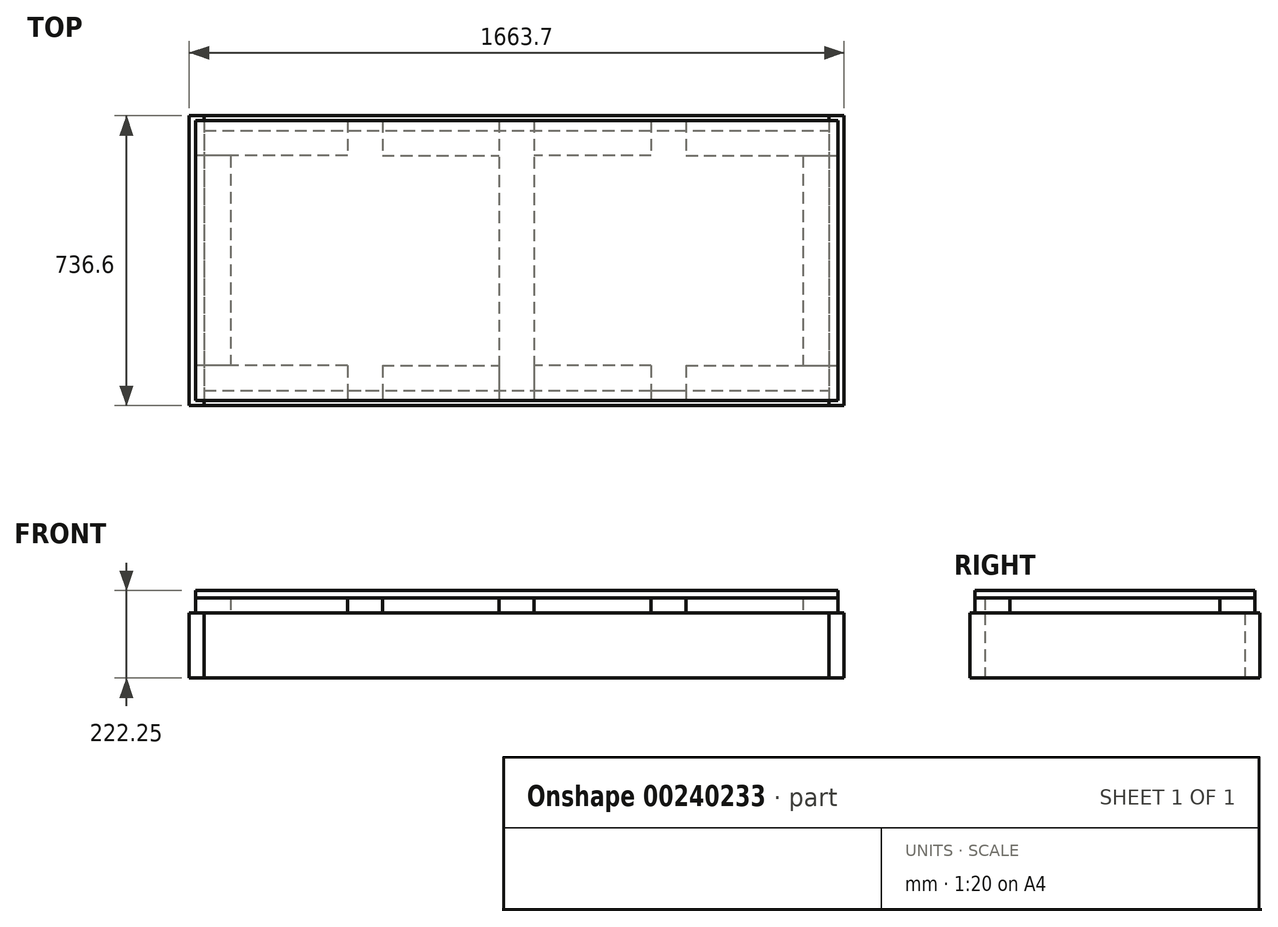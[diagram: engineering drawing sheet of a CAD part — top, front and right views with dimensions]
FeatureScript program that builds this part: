
annotation { "Feature Type Name" : "Feature", "Feature Type Description" : "" }
export const myFeature = defineFeature(function(context is Context, id is Id, definition is map)
    precondition{}
    {
        {
            var Q0;
            Q0=qCreatedBy(makeId("Top.planeOp"),FACE);
            var sketch = newSketch(context, id + "F0", { "sketchPlane" : qUnion([Q0])});
            skLineSegment(sketch, "E0.bottom", {"start": v(0, 0) * mm, "end": v(1587.5, 0) * mm});
            skLineSegment(sketch, "E0.top", {"start": v(0, -38.1) * mm, "end": v(1587.5, -38.1) * mm});
            skLineSegment(sketch, "E0.left", {"start": v(0, 0) * mm, "end": v(0, -38.1) * mm});
            skLineSegment(sketch, "E0.right", {"start": v(1587.5, 0) * mm, "end": v(1587.5, -38.1) * mm});
            skLineSegment(sketch, "E1.bottom", {"start": v(0, 698.5) * mm, "end": v(1587.5, 698.5) * mm});
            skLineSegment(sketch, "E1.top", {"start": v(0, 660.4) * mm, "end": v(1587.5, 660.4) * mm});
            skLineSegment(sketch, "E1.left", {"start": v(0, 698.5) * mm, "end": v(0, 660.4) * mm});
            skLineSegment(sketch, "E1.right", {"start": v(1587.5, 698.5) * mm, "end": v(1587.5, 660.4) * mm});
            skLineSegment(sketch, "E2.bottom", {"start": v(1587.5, 698.5) * mm, "end": v(1625.6, 698.5) * mm});
            skLineSegment(sketch, "E2.top", {"start": v(1587.5, -38.1) * mm, "end": v(1625.6, -38.1) * mm});
            skLineSegment(sketch, "E2.left", {"start": v(1587.5, 698.5) * mm, "end": v(1587.5, -38.1) * mm});
            skLineSegment(sketch, "E2.right", {"start": v(1625.6, 698.5) * mm, "end": v(1625.6, -38.1) * mm});
            skLineSegment(sketch, "E3.bottom", {"start": v(0, -38.1) * mm, "end": v(-38.1, -38.1) * mm});
            skLineSegment(sketch, "E3.top", {"start": v(0, 698.5) * mm, "end": v(-38.1, 698.5) * mm});
            skLineSegment(sketch, "E3.left", {"start": v(0, -38.1) * mm, "end": v(0, 698.5) * mm});
            skLineSegment(sketch, "E3.right", {"start": v(-38.1, -38.1) * mm, "end": v(-38.1, 698.5) * mm});
            skSolve(sketch);
        }
        {
            var Q0;
            {var subQ3=sQuery(id+"F0.wireOp",EDGE,"E3.bottom");Q0=makeQuery(id+"F0.imprint","IMPRINT",FACE,{"disambiguationData":[TD([[makeQuery(id+"F0.imprint","IMPRINT",EDGE,{"derivedFrom":subQ3}),-1.0]])]});}
            extrude(context, id + "F1", {"entities" : qUnion([Q0]), "endBound" : BoundingType.SYMMETRIC, "depth" : 165.1 * mm});
        }
        {
            var Q0;
            {var subQ0=sQuery(id+"F0.wireOp",EDGE,"E1.bottom");Q0=makeQuery(id+"F0.imprint","IMPRINT",FACE,{"disambiguationData":[TD([[makeQuery(id+"F0.imprint","IMPRINT",EDGE,{"derivedFrom":subQ0}),-1.0]])]});}
            extrude(context, id + "F2", {"entities" : qUnion([Q0]), "endBound" : BoundingType.SYMMETRIC, "depth" : 165.1 * mm});
        }
        {
            var Q0;
            {var subQ0=sQuery(id+"F0.wireOp",EDGE,"E0.bottom");Q0=makeQuery(id+"F0.imprint","IMPRINT",FACE,{"disambiguationData":[TD([[makeQuery(id+"F0.imprint","IMPRINT",EDGE,{"derivedFrom":subQ0}),-1.0]])]});}
            extrude(context, id + "F3", {"entities" : qUnion([Q0]), "endBound" : BoundingType.SYMMETRIC, "depth" : 165.1 * mm});
        }
        {
            var Q0;
            {var subQ3=sQuery(id+"F0.wireOp",EDGE,"E2.bottom");Q0=makeQuery(id+"F0.imprint","IMPRINT",FACE,{"disambiguationData":[TD([[makeQuery(id+"F0.imprint","IMPRINT",EDGE,{"derivedFrom":subQ3}),-1.0]])]});}
            extrude(context, id + "F4", {"entities" : qUnion([Q0]), "endBound" : BoundingType.SYMMETRIC, "depth" : 165.1 * mm});
        }
        {
            var Q0;
            Q0=makeQuery(id+"F3.opExtrude","CAP_FACE",FACE,{"disambiguationData":[OSD([sQuery(id+"F0.wireOp",EDGE,"E0.bottom"),sQuery(id+"F0.wireOp",EDGE,"E0.top"),sQuery(id+"F0.wireOp",EDGE,"E2.left"),sQuery(id+"F0.wireOp",EDGE,"E3.left")])],"isStart":false});
            var sketch = newSketch(context, id + "F5", { "sketchPlane" : qUnion([Q0])});
            skLineSegment(sketch, "E4.0", {"start": v(-22.23, -25.4) * mm, "end": v(-22.23, 685.8) * mm});
            skLineSegment(sketch, "E4.1", {"start": v(1609.73, -25.4) * mm, "end": v(-22.23, -25.4) * mm});
            skLineSegment(sketch, "E4.2", {"start": v(1609.73, -25.4) * mm, "end": v(1609.73, 685.8) * mm});
            skLineSegment(sketch, "E4.3", {"start": v(1609.73, 685.8) * mm, "end": v(-22.23, 685.8) * mm});
            skLineSegment(sketch, "E5", {"start": v(66.67, 596.9) * mm, "end": v(66.67, 63.5) * mm});
            skLineSegment(sketch, "E6.bottom", {"start": v(452.44, 685.8) * mm, "end": v(363.54, 685.8) * mm});
            skPoint(sketch, "E6.middle", {"position": v(793.75, 330.2) * mm});
            skLineSegment(sketch, "E7.right", {"start": v(749.3, 685.8) * mm, "end": v(749.3, -25.4) * mm});
            skLineSegment(sketch, "E8.trimOffspring", {"start": v(363.54, 63.5) * mm, "end": v(-22.23, 63.5) * mm});
            skLineSegment(sketch, "E9", {"start": v(363.54, 685.8) * mm, "end": v(363.54, -25.4) * mm});
            skLineSegment(sketch, "E10", {"start": v(452.44, 685.8) * mm, "end": v(452.44, -25.4) * mm});
            skLineSegment(sketch, "E11", {"start": v(363.54, 596.9) * mm, "end": v(-22.23, 596.9) * mm});
            skLineSegment(sketch, "E12", {"start": v(452.44, 596.9) * mm, "end": v(749.3, 596.9) * mm});
            skLineSegment(sketch, "E13", {"start": v(452.44, 63.5) * mm, "end": v(749.3, 63.5) * mm});
            skLineSegment(sketch, "E14", {"start": v(793.75, 685.8) * mm, "end": v(793.75, -25.4) * mm, "construction": true});
            skLineSegment(sketch, "E15.MirrorCS", {"start": v(1135.06, 685.8) * mm, "end": v(1223.96, 685.8) * mm});
            skLineSegment(sketch, "E16.MirrorCS", {"start": v(1135.06, 685.8) * mm, "end": v(1135.06, -25.4) * mm});
            skLineSegment(sketch, "E17.MirrorCS", {"start": v(1223.96, 685.8) * mm, "end": v(1223.96, -25.4) * mm});
            skLineSegment(sketch, "E18.MirrorCS", {"start": v(838.2, 685.8) * mm, "end": v(838.2, -25.4) * mm});
            skLineSegment(sketch, "E19.MirrorCS", {"start": v(1223.96, 63.5) * mm, "end": v(1609.73, 63.5) * mm});
            skLineSegment(sketch, "E20.MirrorCS", {"start": v(1135.06, 596.9) * mm, "end": v(838.2, 596.9) * mm});
            skLineSegment(sketch, "E21.MirrorCS", {"start": v(1135.06, 63.5) * mm, "end": v(838.2, 63.5) * mm});
            skLineSegment(sketch, "E22.MirrorCS", {"start": v(1223.96, 596.9) * mm, "end": v(1609.73, 596.9) * mm});
            skLineSegment(sketch, "E23.MirrorCS", {"start": v(1520.83, 596.9) * mm, "end": v(1520.83, 63.5) * mm});
            skLineSegment(sketch, "E24", {"start": v(-38.1, 698.5) * mm, "end": v(1625.6, -38.1) * mm, "construction": true});
            skLineSegment(sketch, "E25", {"start": v(-38.1, -38.1) * mm, "end": v(1625.6, 698.5) * mm, "construction": true});
            skLineSegment(sketch, "E26", {"start": v(1609.73, 330.2) * mm, "end": v(-22.23, 330.2) * mm, "construction": true});
            skLineSegment(sketch, "E27", {"start": v(407.99, 685.8) * mm, "end": v(407.99, -25.4) * mm, "construction": true});
            skSolve(sketch);
        }
        {
            var Q0;
            {var subQ5=sQuery(id+"F5.wireOp",EDGE,"E5");Q0=makeQuery(id+"F5.imprint","IMPRINT",FACE,{"disambiguationData":[TD([[makeQuery(id+"F5.imprint","IMPRINT",EDGE,{"derivedFrom":subQ5}),-1.0]])]});}
            extrude(context, id + "F6", {"entities" : qUnion([Q0]), "depth" : 38.1 * mm});
        }
        {
            var Q0;
            {var subQ3=sQuery(id+"F5.wireOp",EDGE,"E6.bottom");Q0=makeQuery(id+"F5.imprint","IMPRINT",FACE,{"disambiguationData":[TD([[makeQuery(id+"F5.imprint","IMPRINT",EDGE,{"derivedFrom":subQ3}),1.0]])]});}
            var Q1;
            {var subQ0=sQuery(id+"F5.wireOp",EDGE,"E9");var subQ1=sQuery(id+"F5.wireOp",EDGE,"E4.1");var subQ2=makeQuery(id+"F5.imprint","INTERSECT",VERTEX,{"derivedFrom":[subQ1,subQ0]});Q1=makeQuery(id+"F5.imprint","IMPRINT",FACE,{"disambiguationData":[TD([[makeQuery(id+"F5.imprint","IMPRINT",EDGE,{"disambiguationData":[TD([[subQ2,1.0]])],"derivedFrom":subQ1}),-1.0]])]});}
            extrude(context, id + "F7", {"entities" : qUnion([Q0, Q1]), "depth" : 38.1 * mm});
        }
        {
            var Q0;
            {var subQ0=sQuery(id+"F5.wireOp",EDGE,"E7.right");var subQ5=sQuery(id+"F5.wireOp",EDGE,"E4.3");var subQ6=makeQuery(id+"F5.imprint","INTERSECT",VERTEX,{"derivedFrom":[subQ5,subQ0]});Q0=makeQuery(id+"F5.imprint","IMPRINT",FACE,{"disambiguationData":[TD([[makeQuery(id+"F5.imprint","IMPRINT",EDGE,{"disambiguationData":[TD([[subQ6,1.0]])],"derivedFrom":subQ5}),1.0]])]});}
            var Q1;
            {var subQ0=sQuery(id+"F5.wireOp",EDGE,"E7.right");var subQ1=sQuery(id+"F5.wireOp",EDGE,"E4.1");var subQ2=makeQuery(id+"F5.imprint","INTERSECT",VERTEX,{"derivedFrom":[subQ1,subQ0]});Q1=makeQuery(id+"F5.imprint","IMPRINT",FACE,{"disambiguationData":[TD([[makeQuery(id+"F5.imprint","IMPRINT",EDGE,{"disambiguationData":[TD([[subQ2,1.0]])],"derivedFrom":subQ1}),-1.0]])]});}
            extrude(context, id + "F8", {"entities" : qUnion([Q0, Q1]), "depth" : 38.1 * mm});
        }
        {
            var Q0;
            {var subQ6=sQuery(id+"F5.wireOp",EDGE,"E15.MirrorCS");Q0=makeQuery(id+"F5.imprint","IMPRINT",FACE,{"disambiguationData":[TD([[makeQuery(id+"F5.imprint","IMPRINT",EDGE,{"derivedFrom":subQ6}),-1.0]])]});}
            var Q1;
            {var subQ0=sQuery(id+"F5.wireOp",EDGE,"E16.MirrorCS");var subQ1=sQuery(id+"F5.wireOp",EDGE,"E4.1");var subQ2=makeQuery(id+"F5.imprint","INTERSECT",VERTEX,{"derivedFrom":[subQ1,subQ0]});Q1=makeQuery(id+"F5.imprint","IMPRINT",FACE,{"disambiguationData":[TD([[makeQuery(id+"F5.imprint","IMPRINT",EDGE,{"disambiguationData":[TD([[subQ2,1.0]])],"derivedFrom":subQ1}),-1.0]])]});}
            extrude(context, id + "F9", {"entities" : qUnion([Q0, Q1]), "depth" : 38.1 * mm});
        }
        {
            var Q0;
            {var subQ5=sQuery(id+"F5.wireOp",EDGE,"E23.MirrorCS");Q0=makeQuery(id+"F5.imprint","IMPRINT",FACE,{"disambiguationData":[TD([[makeQuery(id+"F5.imprint","IMPRINT",EDGE,{"derivedFrom":subQ5}),1.0]])]});}
            extrude(context, id + "F10", {"entities" : qUnion([Q0]), "depth" : 38.1 * mm});
        }
        {
            var Q0;
            {var subQ1=sQuery(id+"F5.wireOp",EDGE,"E4.3");var subQ5=sQuery(id+"F5.wireOp",EDGE,"E4.0");var subQ6=makeQuery(id+"F5.imprint","INTERSECT",VERTEX,{"derivedFrom":[subQ5,subQ1]});Q0=makeQuery(id+"F5.imprint","IMPRINT",FACE,{"disambiguationData":[TD([[makeQuery(id+"F5.imprint","IMPRINT",EDGE,{"disambiguationData":[TD([[subQ6,1.0]])],"derivedFrom":subQ5}),-1.0]])]});}
            var Q1;
            {var subQ5=sQuery(id+"F5.wireOp",EDGE,"E12");Q1=makeQuery(id+"F5.imprint","IMPRINT",FACE,{"disambiguationData":[TD([[makeQuery(id+"F5.imprint","IMPRINT",EDGE,{"derivedFrom":subQ5}),1.0]])]});}
            var Q2;
            {var subQ5=sQuery(id+"F5.wireOp",EDGE,"E20.MirrorCS");Q2=makeQuery(id+"F5.imprint","IMPRINT",FACE,{"disambiguationData":[TD([[makeQuery(id+"F5.imprint","IMPRINT",EDGE,{"derivedFrom":subQ5}),-1.0]])]});}
            var Q3;
            {var subQ4=sQuery(id+"F5.wireOp",EDGE,"E4.3");var subQ6=sQuery(id+"F5.wireOp",EDGE,"E4.2");var subQ7=makeQuery(id+"F5.imprint","INTERSECT",VERTEX,{"derivedFrom":[subQ4,subQ6]});Q3=makeQuery(id+"F5.imprint","IMPRINT",FACE,{"disambiguationData":[TD([[makeQuery(id+"F5.imprint","IMPRINT",EDGE,{"disambiguationData":[TD([[subQ7,1.0]])],"derivedFrom":subQ6}),1.0]])]});}
            extrude(context, id + "F11", {"entities" : qUnion([Q0, Q1, Q2, Q3]), "depth" : 38.1 * mm});
        }
        {
            var Q0;
            {var subQ1=sQuery(id+"F5.wireOp",EDGE,"qj0oYwkd-f0o2-NH23-ZEer-4dDjqUlUklY0.right");Q0=makeQuery(id+"F5.imprint","IMPRINT",FACE,{"disambiguationData":[TD([[makeQuery(id+"F5.imprint","IMPRINT",EDGE,{"derivedFrom":subQ1}),-1.0]])]});}
            var Q1;
            {var subQ0=sQuery(id+"F5.wireOp",EDGE,"E9");var subQ1=sQuery(id+"F5.wireOp",EDGE,"E4.1");var subQ2=makeQuery(id+"F5.imprint","INTERSECT",VERTEX,{"derivedFrom":[subQ1,subQ0]});Q1=makeQuery(id+"F5.imprint","IMPRINT",FACE,{"disambiguationData":[TD([[makeQuery(id+"F5.imprint","IMPRINT",EDGE,{"disambiguationData":[TD([[subQ2,-1.0]])],"derivedFrom":subQ1}),-1.0]])]});}
            var Q2;
            {var subQ0=sQuery(id+"F5.wireOp",EDGE,"E13");Q2=makeQuery(id+"F5.imprint","IMPRINT",FACE,{"disambiguationData":[TD([[makeQuery(id+"F5.imprint","IMPRINT",EDGE,{"derivedFrom":subQ0}),-1.0]])]});}
            var Q3;
            {var subQ0=sQuery(id+"F5.wireOp",EDGE,"E7.right");var subQ1=sQuery(id+"F5.wireOp",EDGE,"E4.1");var subQ2=makeQuery(id+"F5.imprint","INTERSECT",VERTEX,{"derivedFrom":[subQ1,subQ0]});Q3=makeQuery(id+"F5.imprint","IMPRINT",FACE,{"disambiguationData":[TD([[makeQuery(id+"F5.imprint","IMPRINT",EDGE,{"disambiguationData":[TD([[subQ2,-1.0]])],"derivedFrom":subQ1}),-1.0]])]});}
            var Q4;
            {var subQ0=sQuery(id+"F5.wireOp",EDGE,"E21.MirrorCS");Q4=makeQuery(id+"F5.imprint","IMPRINT",FACE,{"disambiguationData":[TD([[makeQuery(id+"F5.imprint","IMPRINT",EDGE,{"derivedFrom":subQ0}),1.0]])]});}
            var Q5;
            {var subQ0=sQuery(id+"F5.wireOp",EDGE,"E16.MirrorCS");var subQ1=sQuery(id+"F5.wireOp",EDGE,"E4.1");var subQ2=makeQuery(id+"F5.imprint","INTERSECT",VERTEX,{"derivedFrom":[subQ1,subQ0]});Q5=makeQuery(id+"F5.imprint","IMPRINT",FACE,{"disambiguationData":[TD([[makeQuery(id+"F5.imprint","IMPRINT",EDGE,{"disambiguationData":[TD([[subQ2,-1.0]])],"derivedFrom":subQ1}),-1.0]])]});}
            var Q6;
            {var subQ4=sQuery(id+"F5.wireOp",EDGE,"E4.2");var subQ5=sQuery(id+"F5.wireOp",EDGE,"E4.1");var subQ6=makeQuery(id+"F5.imprint","INTERSECT",VERTEX,{"derivedFrom":[subQ5,subQ4]});Q6=makeQuery(id+"F5.imprint","IMPRINT",FACE,{"disambiguationData":[TD([[makeQuery(id+"F5.imprint","IMPRINT",EDGE,{"disambiguationData":[TD([[subQ6,-1.0]])],"derivedFrom":subQ5}),-1.0]])]});}
            var Q7;
            {var subQ0=sQuery(id+"F5.wireOp",EDGE,"E17.MirrorCS");var subQ1=sQuery(id+"F5.wireOp",EDGE,"E4.1");var subQ2=makeQuery(id+"F5.imprint","INTERSECT",VERTEX,{"derivedFrom":[subQ1,subQ0]});Q7=makeQuery(id+"F5.imprint","IMPRINT",FACE,{"disambiguationData":[TD([[makeQuery(id+"F5.imprint","IMPRINT",EDGE,{"disambiguationData":[TD([[subQ2,1.0]])],"derivedFrom":subQ1}),-1.0]])]});}
            var Q8;
            {var subQ2=sQuery(id+"F5.wireOp",EDGE,"E4.0");var subQ9=sQuery(id+"F5.wireOp",EDGE,"E4.1");var subQ11=makeQuery(id+"F5.imprint","INTERSECT",VERTEX,{"derivedFrom":[subQ2,subQ9]});Q8=makeQuery(id+"F5.imprint","IMPRINT",FACE,{"disambiguationData":[TD([[makeQuery(id+"F5.imprint","IMPRINT",EDGE,{"disambiguationData":[TD([[subQ11,-1.0]])],"derivedFrom":subQ2}),-1.0]])]});}
            extrude(context, id + "F12", {"entities" : qUnion([Q0, Q1, Q2, Q3, Q4, Q5, Q6, Q7, Q8]), "depth" : 38.1 * mm});
        }
        {
            var Q0;
            Q0=makeQuery(id+"F8.opExtrude","CAP_EDGE",EDGE,{"disambiguationData":[OSD([sQuery(id+"F5.wireOp",EDGE,"E4.3")])],"isStart":false});
            cPoint(context, id + "F13", {"entities" : qUnion([Q0]), "parameter" : 0.5});
        }
        {
            var Q0;
            Q0=makeQuery(id+"F12.opExtrude","CAP_VERTEX",VERTEX,{"disambiguationData":[OSD([sQuery(id+"F5.wireOp",EDGE,"E4.0"),sQuery(id+"F5.wireOp",EDGE,"E4.1")])],"isStart":false});
            var Q1;
            Q1=makeQuery(id+"F12.opExtrude","CAP_VERTEX",VERTEX,{"disambiguationData":[OSD([sQuery(id+"F5.wireOp",EDGE,"E4.1"),sQuery(id+"F5.wireOp",EDGE,"E4.2")])],"isStart":false});
            var Q2;
            Q2 = qCreatedBy(id + "F13" ,VERTEX);
            cPlane(context, id + "F14", {"entities" : qUnion([Q0, Q1, Q2]), "cplaneType" : CPlaneType.THREE_POINT, "offset" : 25.4 * mm, "width" : 152.4 * mm, "height" : 152.4 * mm});
        }
        {
            var Q0;
            Q0=qCreatedBy(id+"F14.planeOp",FACE);
            var sketch = newSketch(context, id + "F15", { "sketchPlane" : qUnion([Q0])});
            skLineSegment(sketch, "E28.bottom", {"start": v(-22.23, -685.8) * mm, "end": v(1609.73, -685.8) * mm});
            skLineSegment(sketch, "E28.top", {"start": v(-22.23, 25.4) * mm, "end": v(1609.73, 25.4) * mm});
            skLineSegment(sketch, "E28.left", {"start": v(-22.23, 25.4) * mm, "end": v(-22.23, -685.8) * mm});
            skLineSegment(sketch, "E28.right", {"start": v(1609.73, 25.4) * mm, "end": v(1609.73, -685.8) * mm});
            skSolve(sketch);
        }
        {
            var Q0;
            Q0=qSketchRegion(id+"F15",true);
            extrude(context, id + "F16", {"entities" : qUnion([Q0]), "oppositeDirection" : true, "depth" : 19.05 * mm});
        }
    });
